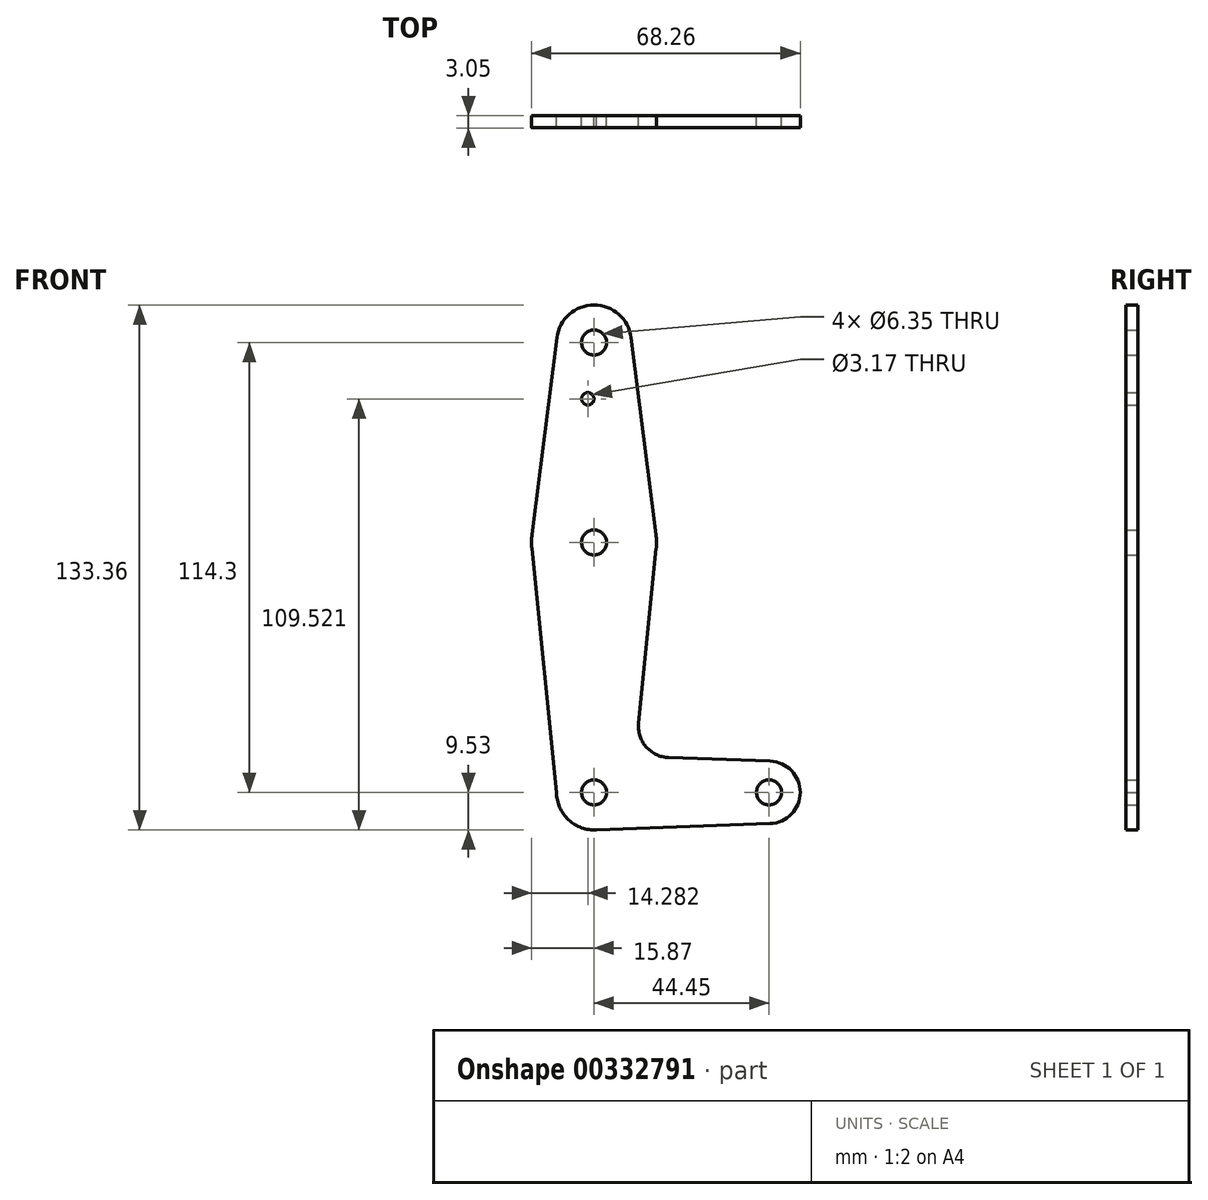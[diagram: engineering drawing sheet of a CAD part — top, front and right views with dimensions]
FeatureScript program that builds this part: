
annotation { "Feature Type Name" : "Feature", "Feature Type Description" : "" }
export const myFeature = defineFeature(function(context is Context, id is Id, definition is map)
    precondition{}
    {
        {
            var Q0;
            Q0=qCreatedBy(makeId("Front.planeOp"),FACE);
            var sketch = newSketch(context, id + "F0", { "sketchPlane" : qUnion([Q0])});
            skLineSegment(sketch, "E0", {"start": v(0, 0) * mm, "end": v(0, 114.3) * mm, "construction": true});
            skCircle(sketch, "E1", {"center": v(0, 0) * mm, "radius": 9.53 * mm});
            skCircle(sketch, "E2", {"center": v(0, 114.3) * mm, "radius": 9.53 * mm});
            skCircle(sketch, "E3", {"center": v(44.45, 0) * mm, "radius": 7.94 * mm});
            skCircle(sketch, "E4", {"center": v(0, 63.5) * mm, "radius": 15.88 * mm});
            skLineSegment(sketch, "E5", {"start": v(9.45, 115.5) * mm, "end": v(15.75, 65.48) * mm});
            skLineSegment(sketch, "E6", {"start": v(15.8, 61.9) * mm, "end": v(11.3, 17.6) * mm});
            skLineSegment(sketch, "E7", {"start": v(18.93, 8.85) * mm, "end": v(44.73, 7.93) * mm});
            skLineSegment(sketch, "E8", {"start": v(-9.53, 0) * mm, "end": v(-15.8, 61.9) * mm});
            skLineSegment(sketch, "E9", {"start": v(0, -9.53) * mm, "end": v(44.73, -7.93) * mm});
            skLineSegment(sketch, "E10", {"start": v(-9.45, 115.5) * mm, "end": v(-15.75, 65.48) * mm});
            skCircle(sketch, "E11", {"center": v(0, 0) * mm, "radius": 3.18 * mm});
            skCircle(sketch, "E12", {"center": v(44.45, 0) * mm, "radius": 3.18 * mm});
            skCircle(sketch, "E13", {"center": v(0, 63.5) * mm, "radius": 3.18 * mm});
            skCircle(sketch, "E14", {"center": v(0, 114.3) * mm, "radius": 3.18 * mm});
            skCircle(sketch, "E15", {"center": v(-1.59, 100) * mm, "radius": 1.59 * mm});
            skArc(sketch, "E16.filletArc", {"start": v(11.3, 17.6) * mm, "mid": v(13.22, 11.57) * mm, "end": v(18.93, 8.85) * mm});
            skLineSegment(sketch, "E17", {"start": v(0, 0) * mm, "end": v(44.45, 0) * mm, "construction": true});
            skSolve(sketch);
        }
        {
            var Q0;
            Q0=qSketchRegion(id+"F0",true);
            extrude(context, id + "F1", {"entities" : qUnion([Q0]), "depth" : 3.05 * mm});
        }
    });
